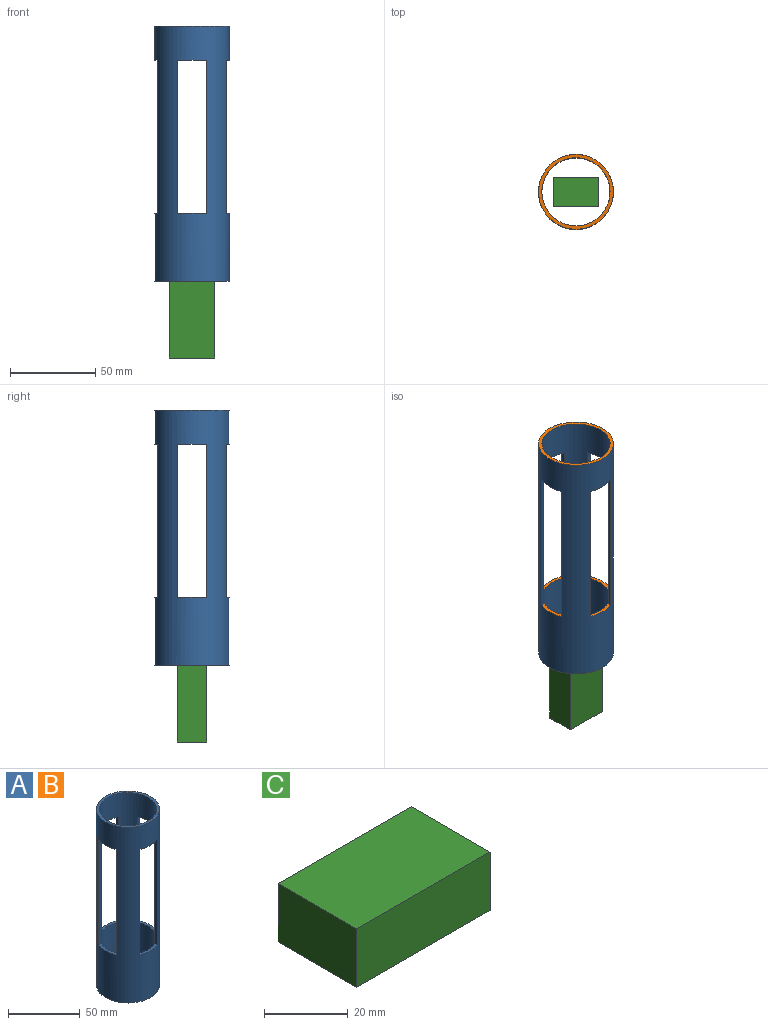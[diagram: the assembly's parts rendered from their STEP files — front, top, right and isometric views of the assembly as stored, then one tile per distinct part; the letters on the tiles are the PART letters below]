
ASSEMBLY  parts=3 mates=1
PART A: 20 faces, bbox 44x44x150 mm
  f0: cylinder r=20mm len=150mm, axis (0,0,1), area 12528.5mm2, adj f2,f3,f4,f5,f6,f7,f8,f9
  f1: cylinder r=22mm len=150mm, axis (0,0,1), area 14451mm2, adj f2,f3,f4,f5,f6,f7,f8,f9
  f2: plane 44x44mm, normal (0,0,-1), area 263.9mm2, adj f0,f1
  f3: plane 44x44mm, normal (0,0,1), area 263.9mm2, adj f0,f1
  f4: plane 90x2.19mm, normal (0,-1,0), area 196.9mm2, adj f0,f1,f5,f7
  f5: plane 17x3.9mm, normal (0,0,-1), area 35mm2, adj f0,f1,f4,f6
  f6: plane 90x2.19mm, normal (0,1,0), area 196.9mm2, adj f0,f1,f5,f7
  f7: plane 17x3.9mm, normal (0,0,1), area 35mm2, adj f0,f1,f4,f6
  f8: plane 90x2.19mm, normal (1,0,0), area 196.9mm2, adj f0,f1,f9,f11
  f9: plane 17x3.9mm, normal (0,0,-1), area 35mm2, adj f0,f1,f8,f10
  f10: plane 90x2.19mm, normal (-1,0,0), area 196.9mm2, adj f0,f1,f9,f11
  f11: plane 17x3.9mm, normal (0,0,1), area 35mm2, adj f0,f1,f8,f10
  f12: plane 90x2.19mm, normal (0,1,0), area 196.9mm2, adj f0,f1,f13,f15
  f13: plane 17x3.9mm, normal (0,0,-1), area 35mm2, adj f0,f1,f12,f14
  f14: plane 90x2.19mm, normal (0,-1,0), area 196.9mm2, adj f0,f1,f13,f15
  f15: plane 17x3.9mm, normal (0,0,1), area 35mm2, adj f0,f1,f12,f14
  f16: plane 90x2.19mm, normal (-1,0,0), area 196.9mm2, adj f0,f1,f17,f19
  f17: plane 17x3.9mm, normal (0,0,-1), area 35mm2, adj f0,f1,f16,f18
  f18: plane 90x2.19mm, normal (1,0,0), area 196.9mm2, adj f0,f1,f17,f19
  f19: plane 17x3.9mm, normal (0,0,1), area 35mm2, adj f0,f1,f16,f18
PART B: same geometry as A
PART C: 6 faces, bbox 45x26.6x17.1 mm
  f0: plane 44.95x17.07mm, normal (0,1,0), area 767.3mm2, adj f1,f3,f4,f5
  f1: plane 26.55x17.07mm, normal (-1,0,0), area 453.2mm2, adj f0,f2,f4,f5
  f2: plane 44.95x17.07mm, normal (0,-1,0), area 767.3mm2, adj f1,f3,f4,f5
  f3: plane 26.55x17.07mm, normal (1,0,0), area 453.2mm2, adj f0,f2,f4,f5
  f4: plane 44.95x26.55mm, normal (0,0,1), area 1193.4mm2, adj f0,f1,f2,f3
  f5: plane 44.95x26.55mm, normal (0,0,-1), area 1193.4mm2, adj f0,f1,f2,f3
PLACE A at identity
PLACE B at identity
PLACE C rot(axis=(-0.58,0.58,0.58),120deg) t=(131.22,-8.54,-22.47)mm
MATE fastened C.f1 <-> A.f0  axis (0,0,1) through (0,0,0)mm
